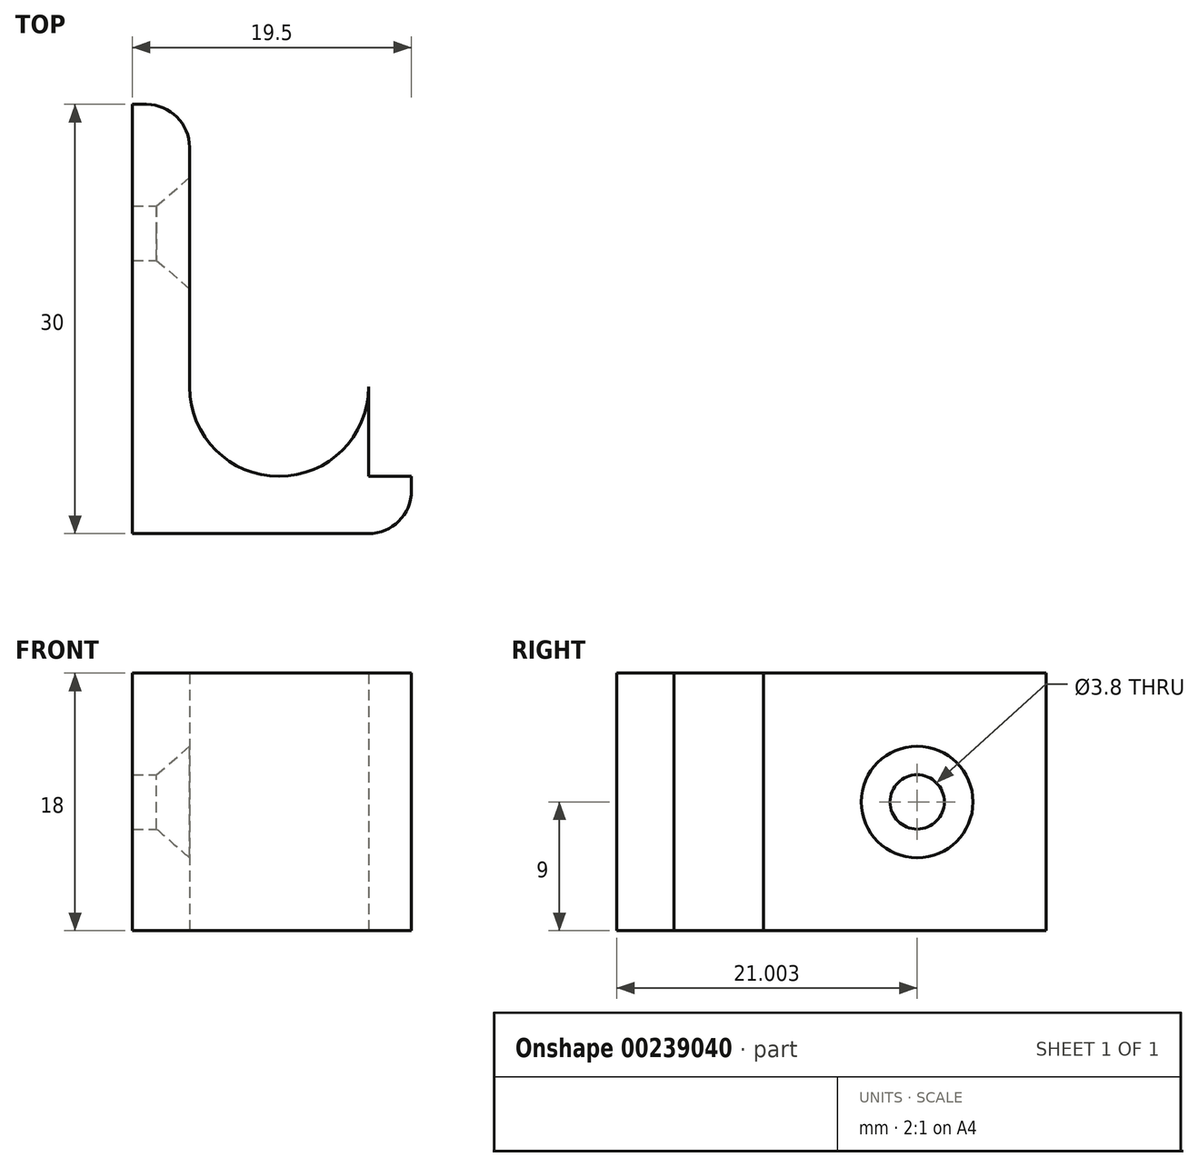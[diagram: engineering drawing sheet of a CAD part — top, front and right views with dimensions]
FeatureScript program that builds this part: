
annotation { "Feature Type Name" : "Feature", "Feature Type Description" : "" }
export const myFeature = defineFeature(function(context is Context, id is Id, definition is map)
    precondition{}
    {
        {
            var Q0;
            Q0=qCreatedBy(makeId("Top.planeOp"),FACE);
            var sketch = newSketch(context, id + "F0", { "sketchPlane" : qUnion([Q0])});
            skLineSegment(sketch, "E0.bottom", {"start": v(-4, 43.08) * mm, "end": v(-3, 43.08) * mm});
            skLineSegment(sketch, "E0.top", {"start": v(-4, 13.08) * mm, "end": v(0, 13.08) * mm});
            skLineSegment(sketch, "E0.left", {"start": v(-4, 43.08) * mm, "end": v(-4, 13.08) * mm});
            skLineSegment(sketch, "E0.right", {"start": v(0, 40.08) * mm, "end": v(0, 13.08) * mm});
            skLineSegment(sketch, "E1.bottom", {"start": v(0, 13.08) * mm, "end": v(12.5, 13.08) * mm});
            skLineSegment(sketch, "E1.top", {"start": v(0, 17.08) * mm, "end": v(15.5, 17.08) * mm});
            skLineSegment(sketch, "E1.left", {"start": v(0, 13.08) * mm, "end": v(0, 17.08) * mm});
            skLineSegment(sketch, "E1.right", {"start": v(15.5, 16.08) * mm, "end": v(15.5, 17.08) * mm});
            skLineSegment(sketch, "E2.bottom", {"start": v(14, 31.08) * mm, "end": v(14, 31.08) * mm});
            skLineSegment(sketch, "E2.top", {"start": v(15.5, 17.08) * mm, "end": v(12.5, 17.08) * mm});
            skLineSegment(sketch, "E2.left", {"start": v(15.5, 29.58) * mm, "end": v(15.5, 17.08) * mm});
            skLineSegment(sketch, "E2.right", {"start": v(12.5, 29.58) * mm, "end": v(12.5, 17.08) * mm});
            skPoint(sketch, "E3.visualSharp", {"position": v(12.5, 31.08) * mm});
            skArc(sketch, "E3.filletArc", {"start": v(14, 31.08) * mm, "mid": v(12.94, 30.64) * mm, "end": v(12.5, 29.58) * mm});
            skPoint(sketch, "E4.visualSharp", {"position": v(15.5, 31.08) * mm});
            skArc(sketch, "E4.filletArc", {"start": v(15.5, 29.58) * mm, "mid": v(15.06, 30.64) * mm, "end": v(14, 31.08) * mm});
            skPoint(sketch, "E5.visualSharp", {"position": v(0, 43.08) * mm});
            skArc(sketch, "E5.filletArc", {"start": v(0, 40.08) * mm, "mid": v(-0.88, 42.2) * mm, "end": v(-3, 43.08) * mm});
            skArc(sketch, "E6", {"start": v(0, 23.33) * mm, "mid": v(6.25, 17.08) * mm, "end": v(12.5, 23.33) * mm});
            skArc(sketch, "E7", {"start": v(12.5, 23.33) * mm, "mid": v(6.25, 29.58) * mm, "end": v(0, 23.33) * mm});
            skPoint(sketch, "E8.visualSharp", {"position": v(15.5, 13.08) * mm});
            skArc(sketch, "E8.filletArc", {"start": v(12.5, 13.08) * mm, "mid": v(14.62, 13.96) * mm, "end": v(15.5, 16.08) * mm});
            skSolve(sketch);
        }
        {
            var Q0;
            Q0=makeQuery(id+"F0.imprint","IMPRINT",FACE,{"disambiguationData":[TD([[makeQuery(id+"F0.imprint","IMPRINT",EDGE,{"derivedFrom":sQuery(id+"F0.wireOp",EDGE,"E0.bottom")}),-1.0]])]});
            var Q1;
            {var subQ0=sQuery(id+"F0.wireOp",EDGE,"E1.top");var subQ3=sQuery(id+"F0.wireOp",EDGE,"E6");var subQ5=makeQuery(id+"F0.imprint","INTERSECT",VERTEX,{"derivedFrom":[subQ0,subQ3]});Q1=makeQuery(id+"F0.imprint","IMPRINT",FACE,{"disambiguationData":[TD([[makeQuery(id+"F0.imprint","IMPRINT",EDGE,{"disambiguationData":[TD([[subQ5,1.0]])],"derivedFrom":subQ0}),1.0]])]});}
            var Q2;
            Q2=makeQuery(id+"F0.imprint","IMPRINT",FACE,{"disambiguationData":[TD([[makeQuery(id+"F0.imprint","IMPRINT",EDGE,{"derivedFrom":sQuery(id+"F0.wireOp",EDGE,"E1.bottom")}),1.0]])]});
            var Q3;
            {var subQ1=sQuery(id+"F0.wireOp",EDGE,"E2.top");Q3=makeQuery(id+"F0.imprint","IMPRINT",FACE,{"disambiguationData":[TD([[makeQuery(id+"F0.imprint","IMPRINT",EDGE,{"derivedFrom":subQ1}),-1.0]])]});}
            var Q4;
            {var subQ1=sQuery(id+"F0.wireOp",EDGE,"E1.top");var subQ3=sQuery(id+"F0.wireOp",EDGE,"E6");var subQ4=makeQuery(id+"F0.imprint","INTERSECT",VERTEX,{"derivedFrom":[subQ1,subQ3]});Q4=makeQuery(id+"F0.imprint","IMPRINT",FACE,{"disambiguationData":[TD([[makeQuery(id+"F0.imprint","IMPRINT",EDGE,{"disambiguationData":[TD([[subQ4,-1.0]])],"derivedFrom":subQ1}),1.0]])]});}
            extrude(context, id + "F1", {"entities" : qUnion([Q0, Q1, Q2, Q3, Q4]), "depth" : 18 * mm});
        }
        {
            var Q0;
            Q0=qCreatedBy(makeId("Right.planeOp"),FACE);
            var sketch = newSketch(context, id + "F2", { "sketchPlane" : qUnion([Q0])});
            skLineSegment(sketch, "E9.bottom", {"start": v(40.08, 18) * mm, "end": v(23.33, 18) * mm});
            skLineSegment(sketch, "E9.top", {"start": v(40.08, 0) * mm, "end": v(23.33, 0) * mm});
            skLineSegment(sketch, "E9.left", {"start": v(40.08, 18) * mm, "end": v(40.08, 0) * mm});
            skLineSegment(sketch, "E9.right", {"start": v(23.33, 18) * mm, "end": v(23.33, 0) * mm});
            skLineSegment(sketch, "E10", {"start": v(40.08, 9) * mm, "end": v(23.33, 9) * mm});
            skPoint(sketch, "E11", {"position": v(34.08, 9) * mm});
            skSolve(sketch);
        }
        {
            var Q0;
            Q0=sQuery(id+"F2.wireOp",VERTEX,"E11");
            var Q1;
            Q1=makeQuery(id+"F1.opExtrude","SWEPT_BODY",BODY,{"disambiguationData":[OSD([sQuery(id+"F0.wireOp",EDGE,"E0.bottom"),sQuery(id+"F0.wireOp",EDGE,"E0.top"),sQuery(id+"F0.wireOp",EDGE,"E0.left"),sQuery(id+"F0.wireOp",EDGE,"E0.right"),sQuery(id+"F0.wireOp",EDGE,"E1.bottom"),sQuery(id+"F0.wireOp",EDGE,"E1.right"),sQuery(id+"F0.wireOp",EDGE,"E2.left"),sQuery(id+"F0.wireOp",EDGE,"E2.right"),sQuery(id+"F0.wireOp",EDGE,"E3.filletArc"),sQuery(id+"F0.wireOp",EDGE,"E4.filletArc"),sQuery(id+"F0.wireOp",EDGE,"E5.filletArc"),sQuery(id+"F0.wireOp",EDGE,"E6"),sQuery(id+"F0.wireOp",EDGE,"E8.filletArc")])]});
            hole(context, id + "F3", {"style" : HoleStyle.C_SINK, "endStyle" : HoleEndStyle.THROUGH, "standardTappedOrClearance" : lookupTablePath({ "standard" : "ANSI", "fit" : "Normal (ASME)", "size" : "#6", "type" : "Clearance" }), "standardBlindInLast" : lookupTablePath({ "fit" : "Free", "standard" : "ANSI", "size" : "#6", "type" : "Clearance" }), "holeDiameter" : 3.8 * mm, "cSinkDiameter" : 7.8 * mm, "cSinkAngle" : 82 * degree, "startFromSketch" : true, "locations" : qUnion([Q0]), "scope" : qUnion([Q1]), "isTappedThrough" : true});
        }
    });
